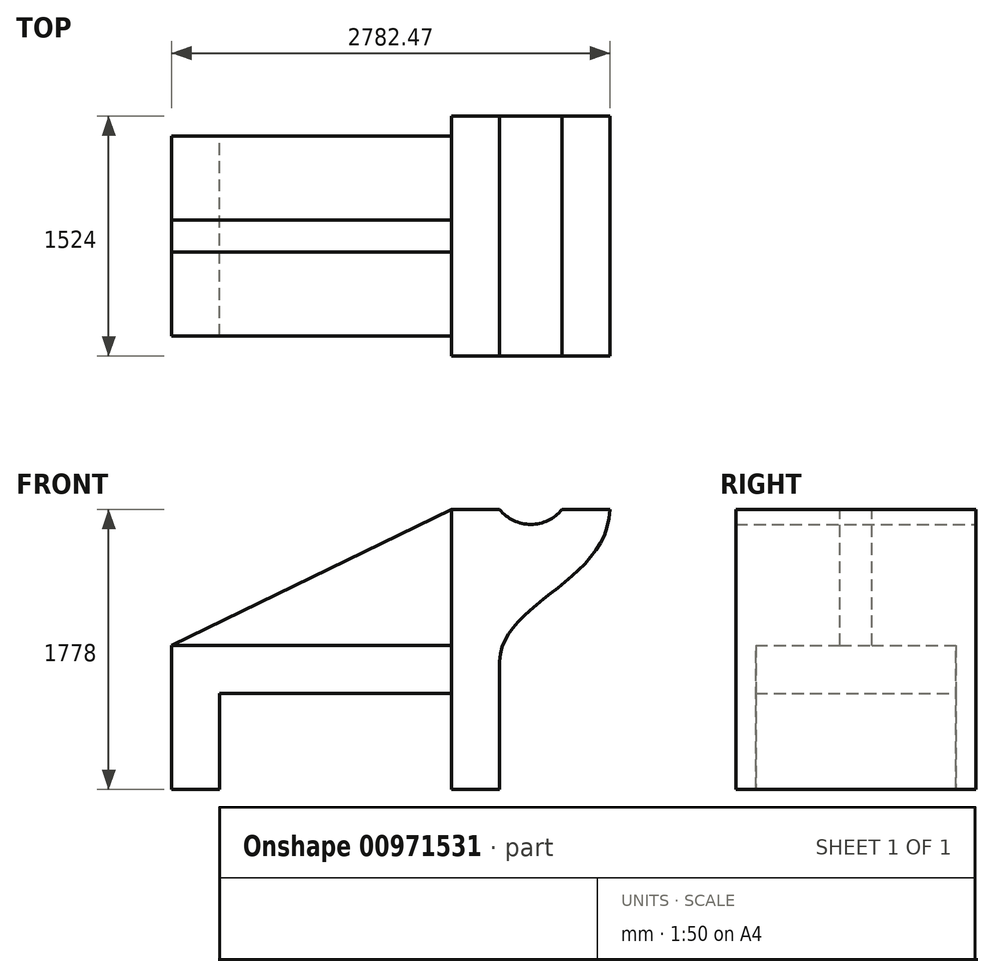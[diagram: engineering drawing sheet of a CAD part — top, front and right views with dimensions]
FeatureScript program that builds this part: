
annotation { "Feature Type Name" : "Feature", "Feature Type Description" : "" }
export const myFeature = defineFeature(function(context is Context, id is Id, definition is map)
    precondition{}
    {
        {
            var Q0;
            Q0=qCreatedBy(makeId("Front.planeOp"),FACE);
            var sketch = newSketch(context, id + "F0", { "sketchPlane" : qUnion([Q0])});
            skLineSegment(sketch, "E0", {"start": v(0, 0) * mm, "end": v(0, 914.4) * mm});
            skLineSegment(sketch, "E1", {"start": v(0, 914.4) * mm, "end": v(1778, 914.4) * mm});
            skLineSegment(sketch, "E2", {"start": v(1778, 914.4) * mm, "end": v(1778, 609.6) * mm});
            skLineSegment(sketch, "E3", {"start": v(1778, 609.6) * mm, "end": v(304.8, 609.6) * mm});
            skLineSegment(sketch, "E4", {"start": v(304.8, 609.6) * mm, "end": v(304.8, 0) * mm});
            skLineSegment(sketch, "E5", {"start": v(304.8, 0) * mm, "end": v(0, 0) * mm});
            skLineSegment(sketch, "E6", {"start": v(1778, 0) * mm, "end": v(1778, 1778) * mm});
            skLineSegment(sketch, "E7", {"start": v(1778, 1778) * mm, "end": v(2082.8, 1778) * mm});
            skArc(sketch, "E8", {"start": v(2082.8, 1778) * mm, "mid": v(2280.23, 1683.8) * mm, "end": v(2477.67, 1778) * mm});
            skLineSegment(sketch, "E9", {"start": v(2477.67, 1778) * mm, "end": v(2782.47, 1778) * mm});
            skLineSegment(sketch, "E10", {"start": v(1778, 0) * mm, "end": v(2082.8, 0) * mm});
            skLineSegment(sketch, "E11", {"start": v(2082.8, 0) * mm, "end": v(2082.8, 812.8) * mm});
            skFitSpline(sketch, "E12", {"points": [v(2082.8, 812.8) * mm, v(2782.47, 1778) * mm], "startDerivative": vector(0, 1104.57) * mm, "endDerivative": vector(31.06, 1369.06) * mm});
            skLineSegment(sketch, "E13", {"start": v(0, 914.4) * mm, "end": v(1778, 1778) * mm});
            skSolve(sketch);
        }
        {
            var Q0;
            {var subQ0=sQuery(id+"F0.wireOp",EDGE,"E7");Q0=makeQuery(id+"F0.imprint","IMPRINT",FACE,{"disambiguationData":[TD([[makeQuery(id+"F0.imprint","IMPRINT",EDGE,{"derivedFrom":subQ0}),-1.0]])]});}
            extrude(context, id + "F1", {"entities" : qUnion([Q0]), "endBound" : BoundingType.SYMMETRIC, "depth" : 1524 * mm, "offsetDistance" : 25.4 * mm});
        }
        {
            var Q0;
            Q0=makeQuery(id+"F0.imprint","IMPRINT",FACE,{"disambiguationData":[TD([[makeQuery(id+"F0.imprint","IMPRINT",EDGE,{"derivedFrom":sQuery(id+"F0.wireOp",EDGE,"E0")}),-1.0]])]});
            extrude(context, id + "F2", {"entities" : qUnion([Q0]), "operationType" : NewBodyOperationType.ADD, "endBound" : BoundingType.SYMMETRIC, "depth" : 1270 * mm, "offsetDistance" : 25.4 * mm});
        }
        {
            var Q0;
            {var subQ0=sQuery(id+"F0.wireOp",EDGE,"E1");Q0=makeQuery(id+"F0.imprint","IMPRINT",FACE,{"disambiguationData":[TD([[makeQuery(id+"F0.imprint","IMPRINT",EDGE,{"derivedFrom":subQ0}),1.0]])]});}
            extrude(context, id + "F3", {"entities" : qUnion([Q0]), "operationType" : NewBodyOperationType.ADD, "endBound" : BoundingType.SYMMETRIC, "depth" : 203.2 * mm, "offsetDistance" : 25.4 * mm});
        }
    });
